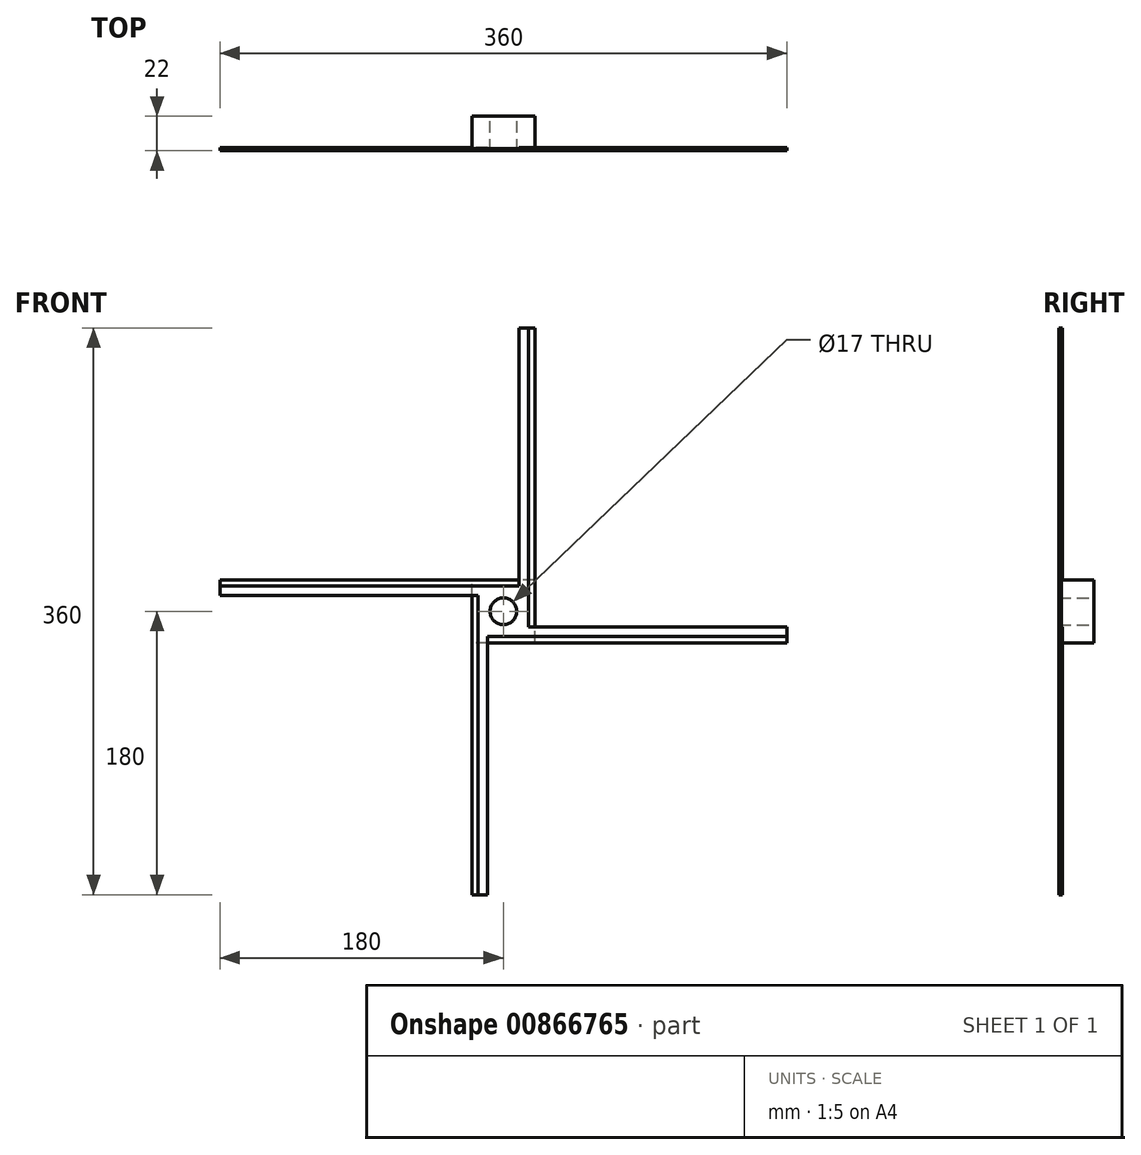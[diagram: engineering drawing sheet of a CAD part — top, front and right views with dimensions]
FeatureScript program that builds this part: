
annotation { "Feature Type Name" : "Feature", "Feature Type Description" : "" }
export const myFeature = defineFeature(function(context is Context, id is Id, definition is map)
    precondition{}
    {
        {
            var Q0;
            Q0=qCreatedBy(makeId("Front.planeOp"),FACE);
            var sketch = newSketch(context, id + "F0", { "sketchPlane" : qUnion([Q0])});
            skLineSegment(sketch, "E0.bottom", {"start": v(20, -20) * mm, "end": v(-20, -20) * mm});
            skLineSegment(sketch, "E0.top", {"start": v(20, 20) * mm, "end": v(-20, 20) * mm});
            skLineSegment(sketch, "E0.left", {"start": v(20, -20) * mm, "end": v(20, 20) * mm});
            skLineSegment(sketch, "E0.right", {"start": v(-20, -20) * mm, "end": v(-20, 20) * mm});
            skPoint(sketch, "E0.middle", {"position": v(0, 0) * mm});
            skLineSegment(sketch, "E1.bottom", {"start": v(-20, 20) * mm, "end": v(-180, 20) * mm});
            skLineSegment(sketch, "E1.top", {"start": v(-20, 10) * mm, "end": v(-180, 10) * mm});
            skLineSegment(sketch, "E1.left", {"start": v(-20, 20) * mm, "end": v(-20, 10) * mm});
            skLineSegment(sketch, "E1.right", {"start": v(-180, 20) * mm, "end": v(-180, 10) * mm});
            skLineSegment(sketch, "E2.bottom", {"start": v(-20, -20) * mm, "end": v(-10, -20) * mm});
            skLineSegment(sketch, "E2.top", {"start": v(-20, -180) * mm, "end": v(-10, -180) * mm});
            skLineSegment(sketch, "E2.left", {"start": v(-20, -20) * mm, "end": v(-20, -180) * mm});
            skLineSegment(sketch, "E2.right", {"start": v(-10, -20) * mm, "end": v(-10, -180) * mm});
            skLineSegment(sketch, "E3.bottom", {"start": v(20, -20) * mm, "end": v(180, -20) * mm});
            skLineSegment(sketch, "E3.top", {"start": v(20, -10) * mm, "end": v(180, -10) * mm});
            skLineSegment(sketch, "E3.left", {"start": v(20, -20) * mm, "end": v(20, -10) * mm});
            skLineSegment(sketch, "E3.right", {"start": v(180, -20) * mm, "end": v(180, -10) * mm});
            skLineSegment(sketch, "E4.bottom", {"start": v(20, 20) * mm, "end": v(10, 20) * mm});
            skLineSegment(sketch, "E4.top", {"start": v(20, 180) * mm, "end": v(10, 180) * mm});
            skLineSegment(sketch, "E4.left", {"start": v(20, 20) * mm, "end": v(20, 180) * mm});
            skLineSegment(sketch, "E4.right", {"start": v(10, 20) * mm, "end": v(10, 180) * mm});
            skCircle(sketch, "E5", {"center": v(0, 0) * mm, "radius": 8.5 * mm});
            skSolve(sketch);
        }
        {
            var Q0;
            Q0=makeQuery(id+"F0.imprint","IMPRINT",FACE,{"disambiguationData":[TD([[makeQuery(id+"F0.imprint","IMPRINT",EDGE,{"derivedFrom":sQuery(id+"F0.wireOp",EDGE,"E4.top")}),1.0]])]});
            var Q1;
            {var subQ0=sQuery(id+"F0.wireOp",EDGE,"E1.bottom");Q1=makeQuery(id+"F0.imprint","IMPRINT",FACE,{"disambiguationData":[TD([[makeQuery(id+"F0.imprint","IMPRINT",EDGE,{"derivedFrom":subQ0}),1.0]])]});}
            var Q2;
            Q2=makeQuery(id+"F0.imprint","IMPRINT",FACE,{"disambiguationData":[TD([[makeQuery(id+"F0.imprint","IMPRINT",EDGE,{"derivedFrom":sQuery(id+"F0.wireOp",EDGE,"E5")}),-1.0]])]});
            var Q3;
            {var subQ0=sQuery(id+"F0.wireOp",EDGE,"E3.bottom");Q3=makeQuery(id+"F0.imprint","IMPRINT",FACE,{"disambiguationData":[TD([[makeQuery(id+"F0.imprint","IMPRINT",EDGE,{"derivedFrom":subQ0}),1.0]])]});}
            var Q4;
            Q4=makeQuery(id+"F0.imprint","IMPRINT",FACE,{"disambiguationData":[TD([[makeQuery(id+"F0.imprint","IMPRINT",EDGE,{"derivedFrom":sQuery(id+"F0.wireOp",EDGE,"E2.top")}),1.0]])]});
            extrude(context, id + "F1", {"entities" : qUnion([Q0, Q1, Q2, Q3, Q4]), "depth" : 2 * mm, "offsetDistance" : 25 * mm});
        }
        {
            var Q0;
            Q0=makeQuery(id+"F0.imprint","IMPRINT",FACE,{"disambiguationData":[TD([[makeQuery(id+"F0.imprint","IMPRINT",EDGE,{"derivedFrom":sQuery(id+"F0.wireOp",EDGE,"E5")}),-1.0]])]});
            extrude(context, id + "F2", {"entities" : qUnion([Q0]), "operationType" : NewBodyOperationType.ADD, "oppositeDirection" : true, "depth" : 20 * mm, "offsetDistance" : 25 * mm});
        }
        {
            var Q0;
            Q0=makeQuery(id+"F1.opExtrude","CAP_EDGE",EDGE,{"disambiguationData":[OSD([sQuery(id+"F0.wireOp",EDGE,"E0.top"),sQuery(id+"F0.wireOp",EDGE,"E1.bottom")])],"isStart":false});
            var Q1;
            Q1=makeQuery(id+"F1.opExtrude","CAP_EDGE",EDGE,{"disambiguationData":[OSD([sQuery(id+"F0.wireOp",EDGE,"E0.left"),sQuery(id+"F0.wireOp",EDGE,"E4.left")])],"isStart":false});
            var Q2;
            Q2=makeQuery(id+"F1.opExtrude","CAP_EDGE",EDGE,{"disambiguationData":[OSD([sQuery(id+"F0.wireOp",EDGE,"E0.bottom"),sQuery(id+"F0.wireOp",EDGE,"E3.bottom")])],"isStart":false});
            var Q3;
            Q3=makeQuery(id+"F1.opExtrude","CAP_EDGE",EDGE,{"disambiguationData":[OSD([sQuery(id+"F0.wireOp",EDGE,"E0.right"),sQuery(id+"F0.wireOp",EDGE,"E2.left")])],"isStart":false});
            chamfer(context, id + "F3", {"entities" : qUnion([Q0, Q1, Q2, Q3]), "chamferType" : ChamferType.OFFSET_ANGLE, "width" : 4 * mm, "oppositeDirection" : false, "angle" : 20 * degree, "tangentPropagation" : true});
        }
    });
